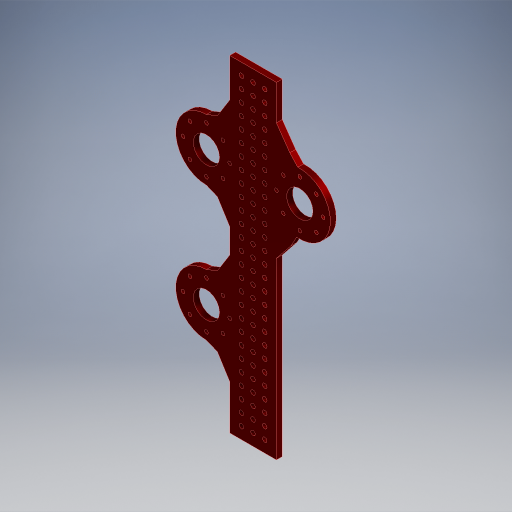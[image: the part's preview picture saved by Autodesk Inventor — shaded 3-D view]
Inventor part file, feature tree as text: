
AUTODESK INVENTOR PART (.ipt)
format: ipt  version: 2024.2 (Build 282272000, 272)  size: 632,832 bytes
history: native  units: in
note: dims shown in document units (in); Inventor stores cm internally (conversion verified against a paired STEP export)
features: other x4, extrude x1, sketch x1, projected_geometry x1
ambient origin geometry x8: Origin, YZ Plane, XZ Plane, XY Plane, X Axis, Y Axis, Z Axis, Center Point
bodies: Body1 (feature_tree)
feature tree (7):
  other  "2024-210-009-Shooter-Gusset-Plate"
  other  "2024-210-008-Shooter-Gusset.ipt"
  extrude  "Extrusion1"  Depth=0.3937in TaperAngle=0.0deg
  other  "2024-210-009-Shooter-Gusset-Plate::2024-210-008-Shooter-Gusset.ipt"
  other  "TaggingFeature1"
  sketch  "Sketch1"  dims[d0=0.3937in d1=0.125in d2=0.0in]
  projected_geometry  "Projected Loop1"
